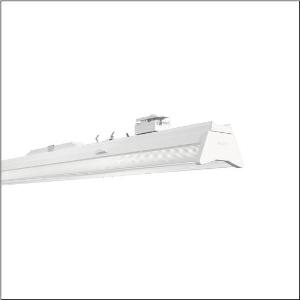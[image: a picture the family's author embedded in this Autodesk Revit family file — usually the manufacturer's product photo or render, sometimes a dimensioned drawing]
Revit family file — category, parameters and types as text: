
# Revit family: licross_r__21_performance_mo_52td167n46xg_c3aa
name_source: partatom
category: Lighting Fixtures
units: mm (PartAtom-declared; Revit-internal decimal feet)

## family parameters
Cut with Voids When Loaded = No
Host = Face
Light Source = No
Part Type = Normal
Room Calculation Point = No
Round Connector Dimension = Use Diameter
Shared = No

## types (1)
- Licross® 21 Performance MO (1 x LED, 6000 lm, 32.4 W, 4000K)
    Apparent Load = 32 VA
    CIE Flux Codes = 66 88 96 79 100
    Color Rendering = 80
    Color Temperature = 4000K
    Default Elevation = 1800 mm
    Description = Licross® 21 Performance MO, luminaire insert, of sheet steel, galvanised, coil coated, white, length: 1.500mm, width: 120mm, height: 123mm, LED rated luminous flux: 6.000lm, light colour: 840, control gear: ON/OFF, with plug, 3-pole, with phase selection, mains connection: 220..240V, AC, 50/60Hz, rated input power: 32W, halogen-free wiring, primary light control with lens, of plastic, primary optical cover: cover, of PMMA, light emission: direct/indirect distribution, primary light characteristic: symmetric, protection rating (complete): IP54, insulation class (complete): insulation class I (protective earthing), certification: CE, ENEC, UKCA, protection symbol: D if used in an environment with non-conductive dust loads with corresponding accessories, impact resistance: IK06, permissible ambient temperature for indoor applications: -35..+50°C, corresponds to IFS (International Featured Standards) requirements for safety and quality in the food industry, reducing of maximum allowable ambient temperature of 5°C with ceiling mounting, LABS conformity tested according to VDMA 24364:2018-05, packaging unit: 1 piece
    Height = 114 mm
    Lamp = 1 x LED
    Lamp Light Flux = 6000 lm
    Lamp Power = 32.4 W
    Lamp count = 1
    Length = 1500 mm
    Luminous efficacy = 185 lm/W
    Manufacturer = Siteco
    ModVariant = No
    Model = 52TD167N46XG
    Mounting Place = Ceiling
    Mounting Type = Pendant
    Number of Poles = 1
    OnlyDefault = Yes
    Power Factor = 1
    Product Name = Licross® 21 Performance MO
    Product group = luminaire insert
    ProductGroupID = 901
    Protection Class = Protection class I
    Protection Degree = IP 54
    RLX_Detail_Level = 1
    RLX_Emergency_Light_Flux = 0 lm
    RLX_Emergency_Type = 0
    RLX_Emergency_Type_DB = No
    RlxData = <blob elided: 30345 chars, md5=cafe5144>
    Socket = socket
    Standby Power = 0 W
    System Light Flux = 6000 lm
    System Power = 32 W
    Type Comments = Product without accessories
    Type Image = l_1256138.jpg
    URL = http://relux.com
    VarID = ---
    Voltage = 0 V
    Weight = 0.00 kg
    Width = 120 mm

## geometry (parser evidence)
native form markers: Blend x4, Sweep x12
no freeform markers — native parametric forms only
